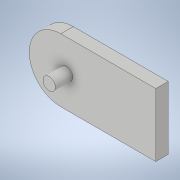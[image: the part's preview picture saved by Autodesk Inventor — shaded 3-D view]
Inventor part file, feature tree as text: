
AUTODESK INVENTOR PART (.ipt)
format: ipt  version: 2022 (Build 260153000, 153)  size: 111,104 bytes
history: native  units: mm
features: extrude x2, sketch x2, fillet x1
ambient origin geometry x8: Origin, YZ Plane, XZ Plane, XY Plane, X Axis, Y Axis, Z Axis, Center Point
bodies: Solid1 (feature_tree)
feature tree (5):
  extrude  "Extrusion1"  Depth=25.4mm
  extrude  "Extrusion2"  Depth=5.0mm
  fillet  "Fillet1"  Radius=15.0mm
  sketch  "Sketch1"  dims[d0=50.8mm d1=25.4mm]
  sketch  "Sketch2"  dims[d2=5.0mm d3=0.0mm d4=5.0mm d5=15.0mm d6=7.0mm d7=0.0mm]
